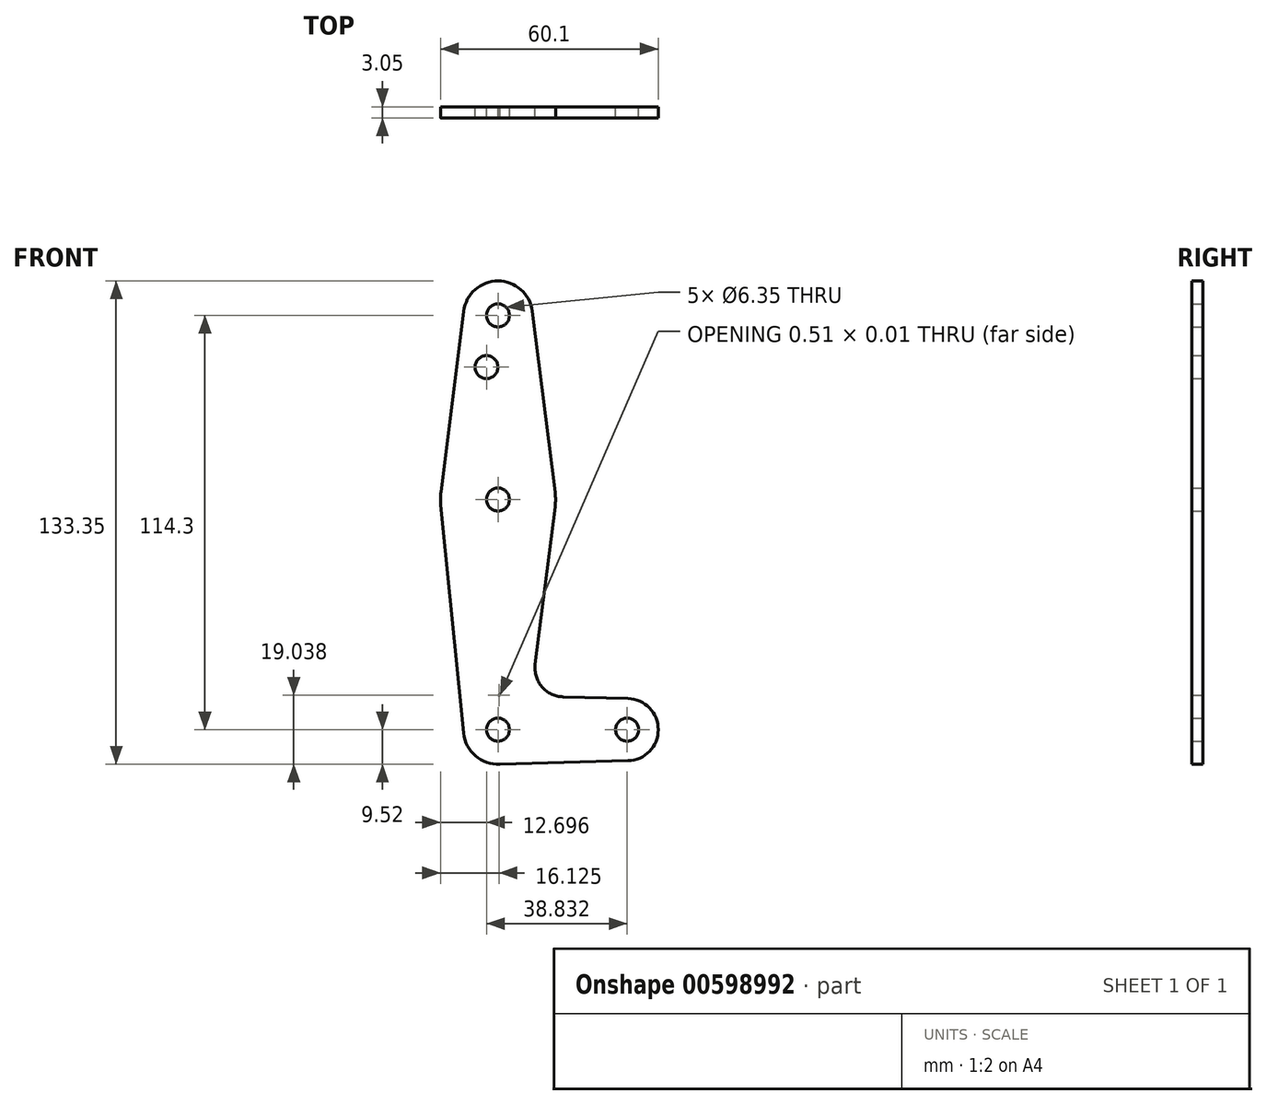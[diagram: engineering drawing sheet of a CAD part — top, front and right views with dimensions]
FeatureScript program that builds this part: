
annotation { "Feature Type Name" : "Feature", "Feature Type Description" : "" }
export const myFeature = defineFeature(function(context is Context, id is Id, definition is map)
    precondition{}
    {
        {
            var Q0;
            Q0=qCreatedBy(makeId("Front.planeOp"),FACE);
            var sketch = newSketch(context, id + "F0", { "sketchPlane" : qUnion([Q0])});
            skLineSegment(sketch, "E0", {"start": v(-17.07, 95.93) * mm, "end": v(-17.07, -18.37) * mm, "construction": true});
            skCircle(sketch, "E1", {"center": v(-17.07, 95.93) * mm, "radius": 9.53 * mm});
            skCircle(sketch, "E2", {"center": v(-17.07, 45.13) * mm, "radius": 15.88 * mm});
            skCircle(sketch, "E3", {"center": v(-17.07, -18.37) * mm, "radius": 9.53 * mm});
            skPoint(sketch, "E4.center.orphan", {"position": v(13.7, -18.37) * mm});
            skPoint(sketch, "E5.orphan", {"position": v(18.59, -18.37) * mm});
            skLineSegment(sketch, "E6", {"start": v(-17.07, -18.37) * mm, "end": v(18.59, -18.37) * mm, "construction": true});
            skCircle(sketch, "E7", {"center": v(18.59, -18.37) * mm, "radius": 8.57 * mm});
            skLineSegment(sketch, "E8", {"start": v(-26.52, 97.12) * mm, "end": v(-32.82, 47.11) * mm});
            skLineSegment(sketch, "E9", {"start": v(-7.62, 97.12) * mm, "end": v(-1.32, 47.11) * mm});
            skLineSegment(sketch, "E10", {"start": v(-1.32, 47.11) * mm, "end": v(-1.32, 43.15) * mm});
            skLineSegment(sketch, "E11", {"start": v(-1.32, 43.15) * mm, "end": v(-6.8, -0.38) * mm});
            skLineSegment(sketch, "E12", {"start": v(-17.07, -8.84) * mm, "end": v(-16.56, -8.86) * mm});
            skLineSegment(sketch, "E13", {"start": v(-17.07, -27.9) * mm, "end": v(18.82, -26.94) * mm});
            skLineSegment(sketch, "E14", {"start": v(-32.82, 47.11) * mm, "end": v(-32.86, 43.54) * mm});
            skCircle(sketch, "E15", {"center": v(-17.07, 95.93) * mm, "radius": 3.18 * mm});
            skCircle(sketch, "E16", {"center": v(-17.07, 45.13) * mm, "radius": 3.18 * mm});
            skCircle(sketch, "E17", {"center": v(-17.07, -18.37) * mm, "radius": 3.18 * mm});
            skCircle(sketch, "E18", {"center": v(18.59, -18.37) * mm, "radius": 3.18 * mm});
            skCircle(sketch, "E19", {"center": v(-20.24, 81.66) * mm, "radius": 3.18 * mm});
            skArc(sketch, "E20", {"start": v(-6.8, -0.38) * mm, "mid": v(-4.95, -6.55) * mm, "end": v(0.87, -9.32) * mm});
            skLineSegment(sketch, "E21.trimOffspring", {"start": v(0.87, -9.32) * mm, "end": v(18.82, -9.8) * mm});
            skPoint(sketch, "E22.end.orphan", {"position": v(-26.64, -18.37) * mm});
            skLineSegment(sketch, "E23", {"start": v(-26.55, -19.32) * mm, "end": v(-32.86, 43.54) * mm});
            skLineSegment(sketch, "E24", {"start": v(-32.86, 43.54) * mm, "end": v(-32.82, 47.11) * mm});
            skSolve(sketch);
        }
        {
            var Q0;
            Q0=qSketchRegion(id+"F0",true);
            extrude(context, id + "F1", {"entities" : qUnion([Q0]), "depth" : 3.05 * mm});
        }
    });
